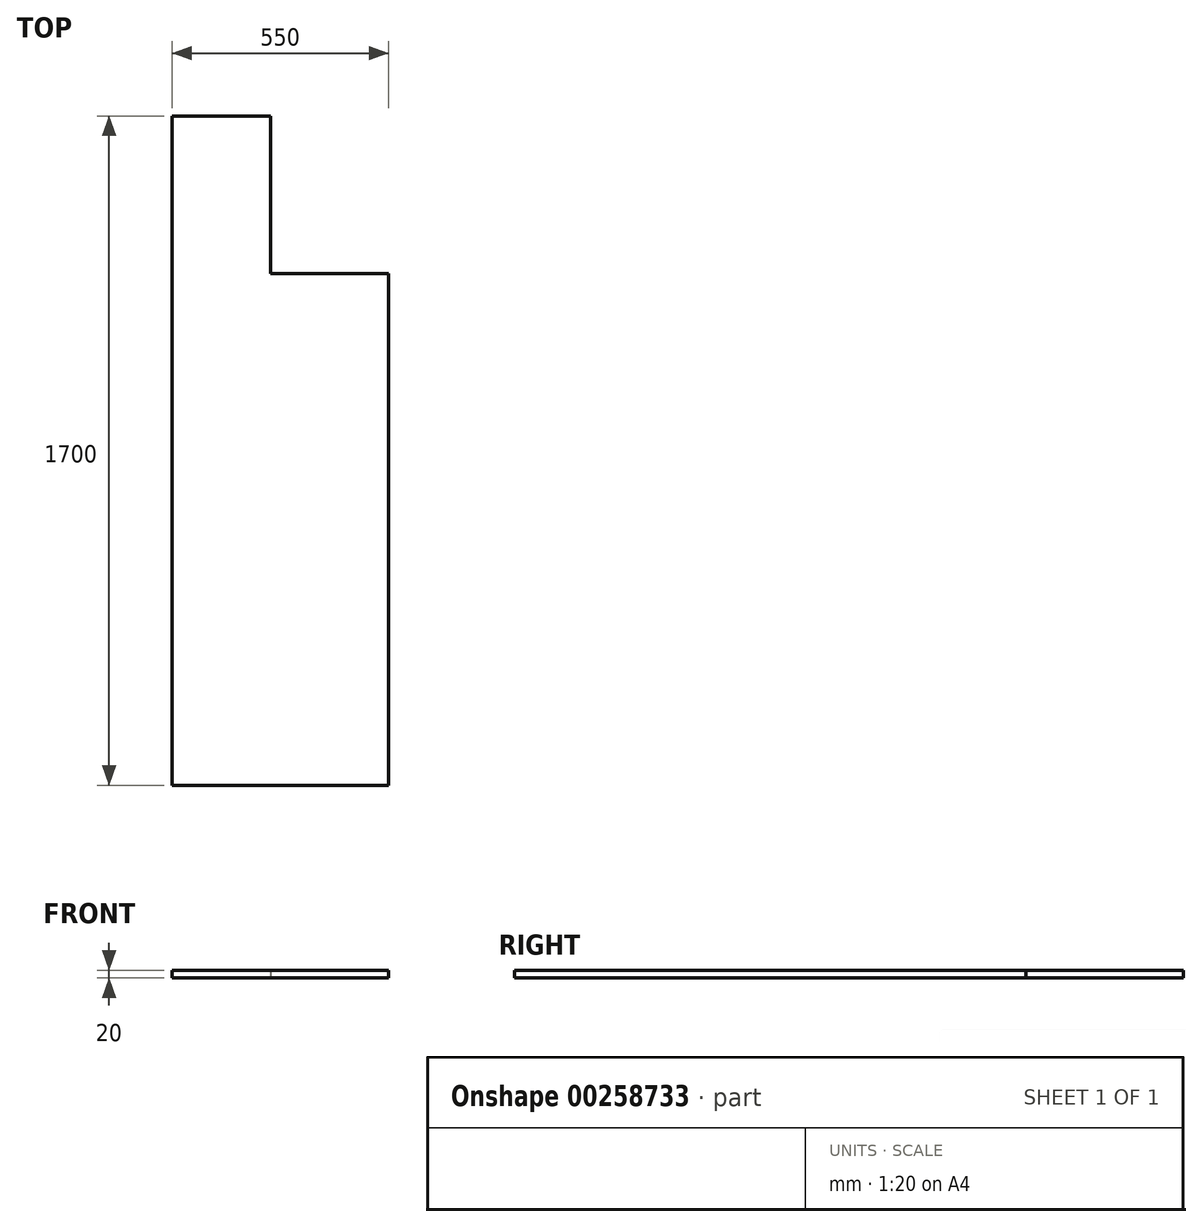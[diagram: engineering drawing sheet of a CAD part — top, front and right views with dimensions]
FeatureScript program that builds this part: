
annotation { "Feature Type Name" : "Feature", "Feature Type Description" : "" }
export const myFeature = defineFeature(function(context is Context, id is Id, definition is map)
    precondition{}
    {
        {
            var Q0;
            Q0=qCreatedBy(makeId("Top.planeOp"),FACE);
            var sketch = newSketch(context, id + "F0", { "sketchPlane" : qUnion([Q0])});
            skLineSegment(sketch, "E0.bottom", {"start": v(0, 0) * mm, "end": v(250, 0) * mm});
            skLineSegment(sketch, "E0.top", {"start": v(0, -1700) * mm, "end": v(550, -1700) * mm});
            skLineSegment(sketch, "E0.left", {"start": v(0, 0) * mm, "end": v(0, -1700) * mm});
            skLineSegment(sketch, "E0.right", {"start": v(550, -400) * mm, "end": v(550, -1700) * mm});
            skLineSegment(sketch, "E1.left", {"start": v(0, 0) * mm, "end": v(0, -400) * mm});
            skLineSegment(sketch, "E1.right", {"start": v(250, 0) * mm, "end": v(250, -400) * mm});
            skLineSegment(sketch, "E2", {"start": v(250, -400) * mm, "end": v(550, -400) * mm});
            skSolve(sketch);
        }
        {
            var Q0;
            Q0=makeQuery(id+"F0.imprint","IMPRINT",FACE,{"disambiguationData":[TD([[makeQuery(id+"F0.imprint","IMPRINT",EDGE,{"derivedFrom":sQuery(id+"F0.wireOp",EDGE,"E0.top")}),1.0]])]});
            extrude(context, id + "F1", {"entities" : qUnion([Q0]), "depth" : 20 * mm});
        }
    });
